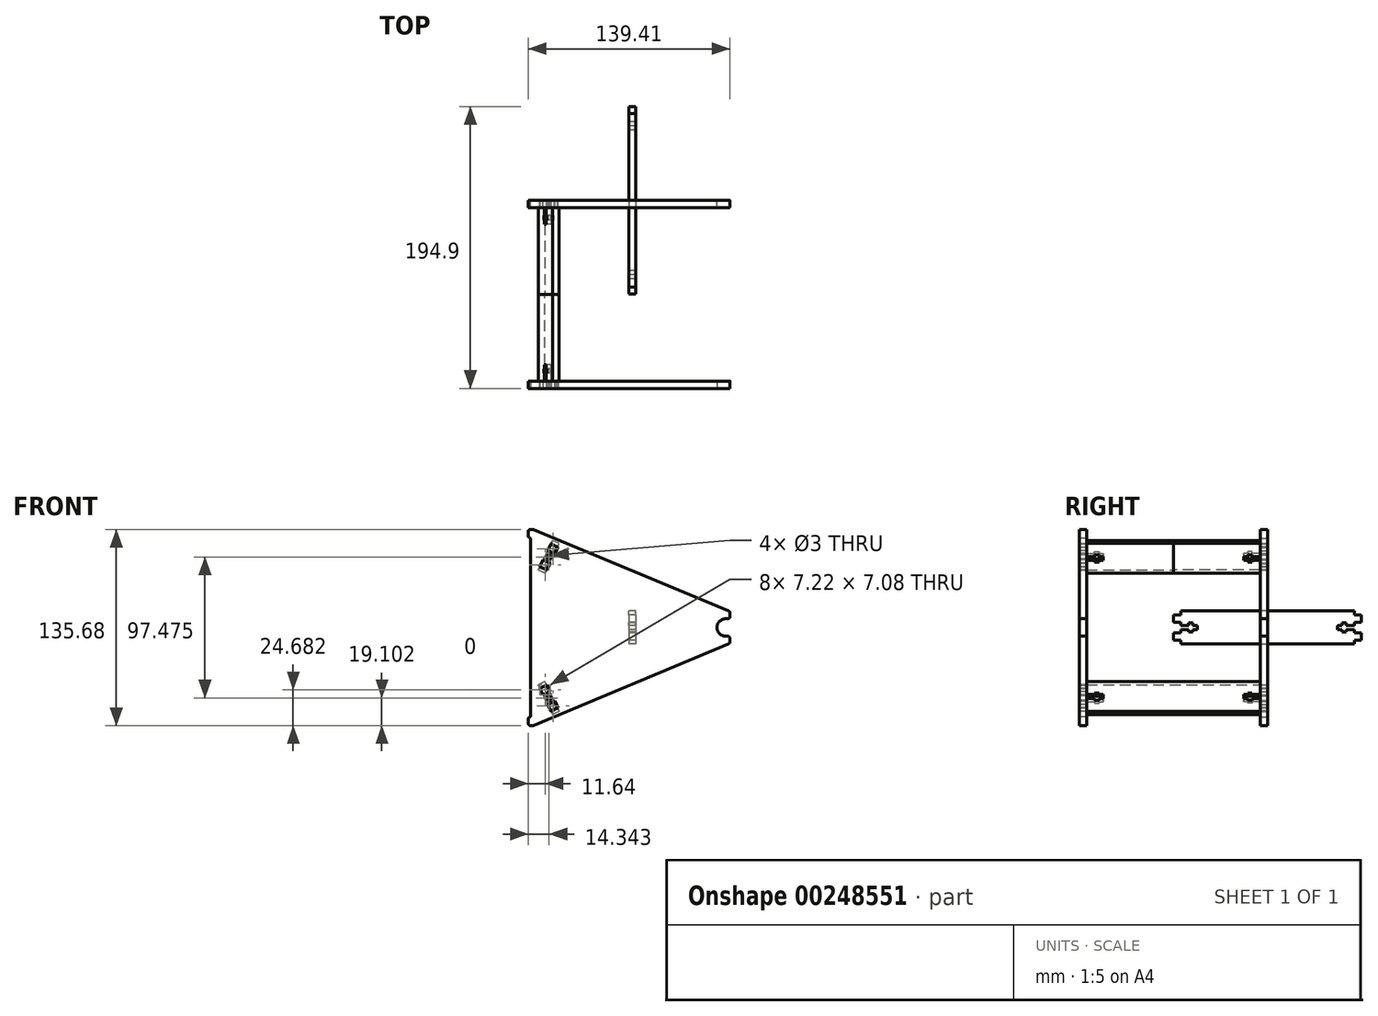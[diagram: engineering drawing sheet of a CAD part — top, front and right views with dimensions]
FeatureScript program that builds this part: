
annotation { "Feature Type Name" : "Feature", "Feature Type Description" : "" }
export const myFeature = defineFeature(function(context is Context, id is Id, definition is map)
    precondition{}
    {
        {
            var Q0;
            Q0=qCreatedBy(makeId("Front.planeOp"),FACE);
            var sketch = newSketch(context, id + "F0", { "sketchPlane" : qUnion([Q0])});
            skLineSegment(sketch, "E0.bottom", {"start": v(70, 69) * mm, "end": v(-70, 69) * mm, "construction": true});
            skLineSegment(sketch, "E0.top", {"start": v(70, -69) * mm, "end": v(-70, -69) * mm, "construction": true});
            skLineSegment(sketch, "E0.left", {"start": v(70, 69) * mm, "end": v(70, -69) * mm, "construction": true});
            skLineSegment(sketch, "E0.right", {"start": v(-70, 69) * mm, "end": v(-70, -69) * mm, "construction": true});
            skPoint(sketch, "E0.middle", {"position": v(0, 0) * mm});
            skLineSegment(sketch, "E1", {"start": v(-67.9, 67.84) * mm, "end": v(-66.66, 67.84) * mm});
            skLineSegment(sketch, "E2", {"start": v(-66.08, 67.72) * mm, "end": v(69.08, 11.47) * mm});
            skArc(sketch, "E3", {"start": v(67, 6) * mm, "mid": v(62.76, 4.24) * mm, "end": v(61, 0) * mm});
            skLineSegment(sketch, "E4", {"start": v(67, 6) * mm, "end": v(68.5, 6) * mm});
            skLineSegment(sketch, "E5", {"start": v(70, 7.5) * mm, "end": v(70, 10.09) * mm});
            skLineSegment(sketch, "E6", {"start": v(73.6, 0) * mm, "end": v(46.28, 0) * mm, "construction": true});
            skPoint(sketch, "E6.startSnap0", {"position": v(70, 0) * mm});
            skCircle(sketch, "E7", {"center": v(67, 0) * mm, "radius": 6 * mm, "construction": true});
            skCircle(sketch, "E8", {"center": v(45.57, 0) * mm, "radius": 27.5 * mm, "construction": true});
            skCircle(sketch, "E9", {"center": v(45.57, 0) * mm, "radius": 100 * mm, "construction": true});
            skLineSegment(sketch, "E10", {"start": v(-69.4, 66.34) * mm, "end": v(-69.4, 63.34) * mm});
            skLineSegment(sketch, "E11", {"start": v(-67.9, 61.84) * mm, "end": v(-67.9, 61.84) * mm});
            skLineSegment(sketch, "E12", {"start": v(-67.9, 61.84) * mm, "end": v(-67.9, 0) * mm});
            skPoint(sketch, "E13.visualSharp", {"position": v(70, 11.09) * mm});
            skArc(sketch, "E13.filletArc", {"start": v(70, 10.09) * mm, "mid": v(69.75, 10.92) * mm, "end": v(69.08, 11.47) * mm});
            skPoint(sketch, "E14.visualSharp", {"position": v(70, 6) * mm});
            skArc(sketch, "E14.filletArc", {"start": v(68.5, 6) * mm, "mid": v(69.56, 6.44) * mm, "end": v(70, 7.5) * mm});
            skPoint(sketch, "E15.visualSharp", {"position": v(-69.4, 67.84) * mm});
            skArc(sketch, "E15.filletArc", {"start": v(-67.9, 67.84) * mm, "mid": v(-68.97, 67.4) * mm, "end": v(-69.4, 66.34) * mm});
            skPoint(sketch, "E16.visualSharp", {"position": v(-69.4, 61.84) * mm});
            skArc(sketch, "E16.filletArc", {"start": v(-69.4, 63.34) * mm, "mid": v(-68.97, 62.27) * mm, "end": v(-67.9, 61.84) * mm});
            skPoint(sketch, "E17.visualSharp", {"position": v(-66.36, 67.84) * mm});
            skArc(sketch, "E17.filletArc", {"start": v(-66.08, 67.72) * mm, "mid": v(-66.37, 67.8) * mm, "end": v(-66.66, 67.84) * mm});
            skLineSegment(sketch, "E18", {"start": v(-48.76, 55.46) * mm, "end": v(-51.02, 50.78) * mm});
            skLineSegment(sketch, "E19", {"start": v(-37.94, 57) * mm, "end": v(-56.8, 18.07) * mm, "construction": true});
            skLineSegment(sketch, "E20", {"start": v(-48.76, 55.46) * mm, "end": v(-53.7, 57.86) * mm});
            skLineSegment(sketch, "E21", {"start": v(-56.43, 39.62) * mm, "end": v(-61.38, 42.02) * mm});
            skLineSegment(sketch, "E22", {"start": v(-53.7, 57.86) * mm, "end": v(-55.97, 53.18) * mm});
            skLineSegment(sketch, "E23", {"start": v(-57.54, 49.94) * mm, "end": v(-52.6, 47.54) * mm, "construction": true});
            skCircle(sketch, "E24", {"center": v(-55.07, 48.74) * mm, "radius": 1.5 * mm});
            skLineSegment(sketch, "E25", {"start": v(-55.97, 53.18) * mm, "end": v(-51.02, 50.78) * mm});
            skLineSegment(sketch, "E26.MirrorCS", {"start": v(-59.11, 46.7) * mm, "end": v(-54.16, 44.3) * mm});
            skLineSegment(sketch, "E27.trimOffspring", {"start": v(-54.16, 44.3) * mm, "end": v(-56.43, 39.62) * mm});
            skLineSegment(sketch, "E28.trimOffspring", {"start": v(-59.11, 46.7) * mm, "end": v(-61.38, 42.02) * mm});
            skLineSegment(sketch, "E29.MirrorCS", {"start": v(-66.08, -67.72) * mm, "end": v(69.08, -11.47) * mm});
            skArc(sketch, "E30.MirrorCS", {"start": v(-66.08, -67.72) * mm, "mid": v(-66.37, -67.8) * mm, "end": v(-66.66, -67.84) * mm});
            skLineSegment(sketch, "E31.MirrorCS", {"start": v(-67.9, -67.84) * mm, "end": v(-66.66, -67.84) * mm});
            skArc(sketch, "E32.MirrorCS", {"start": v(-67.9, -67.84) * mm, "mid": v(-68.97, -67.4) * mm, "end": v(-69.4, -66.34) * mm});
            skLineSegment(sketch, "E33.MirrorCS", {"start": v(-69.4, -66.34) * mm, "end": v(-69.4, -63.34) * mm});
            skArc(sketch, "E34.MirrorCS", {"start": v(-69.4, -63.34) * mm, "mid": v(-68.97, -62.27) * mm, "end": v(-67.9, -61.84) * mm});
            skLineSegment(sketch, "E35.MirrorCS", {"start": v(-67.9, -61.84) * mm, "end": v(-67.9, 0) * mm});
            skLineSegment(sketch, "E36.MirrorCS", {"start": v(70, -7.5) * mm, "end": v(70, -10.09) * mm});
            skArc(sketch, "E37.MirrorCS", {"start": v(70, -10.09) * mm, "mid": v(69.75, -10.92) * mm, "end": v(69.08, -11.47) * mm});
            skArc(sketch, "E38.MirrorCS", {"start": v(68.5, -6) * mm, "mid": v(69.56, -6.44) * mm, "end": v(70, -7.5) * mm});
            skLineSegment(sketch, "E39.MirrorCS", {"start": v(67, -6) * mm, "end": v(68.5, -6) * mm});
            skArc(sketch, "E40.MirrorCS", {"start": v(67, -6) * mm, "mid": v(62.76, -4.24) * mm, "end": v(61, 0) * mm});
            skLineSegment(sketch, "E41.MirrorCS", {"start": v(-57.54, -49.94) * mm, "end": v(-52.6, -47.54) * mm, "construction": true});
            skLineSegment(sketch, "E42.MirrorCS", {"start": v(-59.11, -46.7) * mm, "end": v(-61.38, -42.02) * mm});
            skLineSegment(sketch, "E43.MirrorCS", {"start": v(-53.7, -57.86) * mm, "end": v(-55.97, -53.18) * mm});
            skLineSegment(sketch, "E44.MirrorCS", {"start": v(-59.11, -46.7) * mm, "end": v(-54.16, -44.3) * mm});
            skLineSegment(sketch, "E45.MirrorCS", {"start": v(-55.97, -53.18) * mm, "end": v(-51.02, -50.78) * mm});
            skLineSegment(sketch, "E46.MirrorCS", {"start": v(-56.43, -39.62) * mm, "end": v(-61.38, -42.02) * mm});
            skCircle(sketch, "E47.MirrorC", {"center": v(-55.07, -48.74) * mm, "radius": 1.5 * mm});
            skLineSegment(sketch, "E48.MirrorCS", {"start": v(-48.76, -55.46) * mm, "end": v(-51.02, -50.78) * mm});
            skLineSegment(sketch, "E49.MirrorCS", {"start": v(-54.16, -44.3) * mm, "end": v(-56.43, -39.62) * mm});
            skLineSegment(sketch, "E50.MirrorCS", {"start": v(-48.76, -55.46) * mm, "end": v(-53.7, -57.86) * mm});
            skLineSegment(sketch, "E51", {"start": v(-48.76, 55.46) * mm, "end": v(-56.43, 39.62) * mm, "construction": true});
            skLineSegment(sketch, "E52", {"start": v(-52.6, 47.54) * mm, "end": v(45.57, 0) * mm, "construction": true});
            skSolve(sketch);
        }
        {
            var Q0;
            Q0=qSketchRegion(id+"F0",true);
            extrude(context, id + "F1", {"entities" : qUnion([Q0]), "depth" : 5 * mm});
        }
        {
            var Q0;
            Q0=makeQuery(id+"F1.opExtrude","SWEPT_FACE",FACE,{"disambiguationData":[OSD([sQuery(id+"F0.wireOp",EDGE,"E43.MirrorCS")])]});
            var sketch = newSketch(context, id + "F2", { "sketchPlane" : qUnion([Q0])});
            skLineSegment(sketch, "E53", {"start": v(0, 0) * mm, "end": v(6.16, 29.6) * mm, "construction": true});
            skPoint(sketch, "E53.endSnap0", {"position": v(0, 29.6) * mm});
            skLineSegment(sketch, "E54.0", {"start": v(0, -18.36) * mm, "end": v(0, -21.36) * mm, "construction": true});
            skLineSegment(sketch, "E55", {"start": v(0, -19.86) * mm, "end": v(-5.02, -19.86) * mm, "construction": true});
            skLineSegment(sketch, "E56.1", {"start": v(-0.1, -16.16) * mm, "end": v(-0.1, -11.16) * mm});
            skLineSegment(sketch, "E56.2", {"start": v(-5, -16.16) * mm, "end": v(-0.1, -16.16) * mm});
            skLineSegment(sketch, "E57", {"start": v(-5, -16.16) * mm, "end": v(-5, -18.36) * mm});
            skLineSegment(sketch, "E58", {"start": v(-5, -18.36) * mm, "end": v(-10.6, -18.36) * mm});
            skLineSegment(sketch, "E59", {"start": v(-10.6, -18.36) * mm, "end": v(-10.6, -17.09) * mm});
            skLineSegment(sketch, "E60", {"start": v(-10.6, -17.09) * mm, "end": v(-13.5, -17.09) * mm});
            skLineSegment(sketch, "E61", {"start": v(-13.5, -17.09) * mm, "end": v(-13.5, -18.36) * mm});
            skLineSegment(sketch, "E62", {"start": v(-13.5, -18.36) * mm, "end": v(-16.5, -18.36) * mm});
            skLineSegment(sketch, "E63", {"start": v(-16.5, -18.36) * mm, "end": v(-16.5, -19.86) * mm});
            skLineSegment(sketch, "E64", {"start": v(-0.1, -11.16) * mm, "end": v(-5, -11.16) * mm});
            skLineSegment(sketch, "E65", {"start": v(-5, -11.16) * mm, "end": v(-5, -8.44) * mm});
            skLineSegment(sketch, "E66", {"start": v(-5, -8.44) * mm, "end": v(-65, -8.44) * mm});
            skLineSegment(sketch, "E67.MirrorCS", {"start": v(-13.5, -21.36) * mm, "end": v(-16.5, -21.36) * mm});
            skLineSegment(sketch, "E68.MirrorCS", {"start": v(-10.6, -21.36) * mm, "end": v(-10.6, -22.64) * mm});
            skLineSegment(sketch, "E69.MirrorCS", {"start": v(-5, -28.56) * mm, "end": v(-5, -31.28) * mm});
            skLineSegment(sketch, "E70.MirrorCS", {"start": v(-16.5, -21.36) * mm, "end": v(-16.5, -19.86) * mm});
            skLineSegment(sketch, "E71.MirrorCS", {"start": v(-5, -23.56) * mm, "end": v(-5, -21.36) * mm});
            skLineSegment(sketch, "E72.MirrorCS", {"start": v(-13.5, -22.64) * mm, "end": v(-13.5, -21.36) * mm});
            skLineSegment(sketch, "E73.MirrorCS", {"start": v(-10.6, -22.64) * mm, "end": v(-13.5, -22.64) * mm});
            skLineSegment(sketch, "E74.MirrorCS", {"start": v(0, -21.36) * mm, "end": v(0, -18.36) * mm, "construction": true});
            skLineSegment(sketch, "E75.MirrorCS", {"start": v(-5, -31.28) * mm, "end": v(-65, -31.28) * mm});
            skLineSegment(sketch, "E76.MirrorCS", {"start": v(-0.1, -23.56) * mm, "end": v(-0.1, -28.56) * mm});
            skLineSegment(sketch, "E77.MirrorCS", {"start": v(-5, -21.36) * mm, "end": v(-10.6, -21.36) * mm});
            skLineSegment(sketch, "E78.MirrorCS", {"start": v(-0.1, -28.56) * mm, "end": v(-5, -28.56) * mm});
            skLineSegment(sketch, "E79.MirrorCS", {"start": v(-5, -23.56) * mm, "end": v(-0.1, -23.56) * mm});
            skLineSegment(sketch, "E80", {"start": v(-65, -8.44) * mm, "end": v(-65, -31.28) * mm});
            skSolve(sketch);
        }
        {
            var Q0;
            Q0=qSketchRegion(id+"F2",true);
            extrude(context, id + "F3", {"entities" : qUnion([Q0]), "depth" : 5 * mm});
        }
        {
            var Q0;
            Q0=makeQuery(id+"F3.opExtrude","SWEPT_BODY",BODY,{"disambiguationData":[OSD([sQuery(id+"F2.wireOp",EDGE,"E56.1"),sQuery(id+"F2.wireOp",EDGE,"E56.2"),sQuery(id+"F2.wireOp",EDGE,"E57"),sQuery(id+"F2.wireOp",EDGE,"E58"),sQuery(id+"F2.wireOp",EDGE,"E59"),sQuery(id+"F2.wireOp",EDGE,"E60"),sQuery(id+"F2.wireOp",EDGE,"E61"),sQuery(id+"F2.wireOp",EDGE,"E62"),sQuery(id+"F2.wireOp",EDGE,"E63"),sQuery(id+"F2.wireOp",EDGE,"E64"),sQuery(id+"F2.wireOp",EDGE,"E65"),sQuery(id+"F2.wireOp",EDGE,"E66"),sQuery(id+"F2.wireOp",EDGE,"E67.MirrorCS"),sQuery(id+"F2.wireOp",EDGE,"E68.MirrorCS"),sQuery(id+"F2.wireOp",EDGE,"E69.MirrorCS"),sQuery(id+"F2.wireOp",EDGE,"E70.MirrorCS"),sQuery(id+"F2.wireOp",EDGE,"E71.MirrorCS"),sQuery(id+"F2.wireOp",EDGE,"E72.MirrorCS"),sQuery(id+"F2.wireOp",EDGE,"E73.MirrorCS"),sQuery(id+"F2.wireOp",EDGE,"E75.MirrorCS"),sQuery(id+"F2.wireOp",EDGE,"E76.MirrorCS"),sQuery(id+"F2.wireOp",EDGE,"E77.MirrorCS"),sQuery(id+"F2.wireOp",EDGE,"E78.MirrorCS"),sQuery(id+"F2.wireOp",EDGE,"E79.MirrorCS"),sQuery(id+"F2.wireOp",EDGE,"E80")])]});
            var Q1;
            Q1=qCreatedBy(makeId("Top.planeOp"),FACE);
            mirror(context, id + "F4", {"entities" : qUnion([Q0]), "mirrorPlane" : qUnion([Q1])});
        }
        {
            var Q0;
            Q0=makeQuery(id+"F1.opExtrude","SWEPT_BODY",BODY,{"disambiguationData":[OSD([sQuery(id+"F0.wireOp",EDGE,"E1"),sQuery(id+"F0.wireOp",EDGE,"E2"),sQuery(id+"F0.wireOp",EDGE,"E3"),sQuery(id+"F0.wireOp",EDGE,"E4"),sQuery(id+"F0.wireOp",EDGE,"E5"),sQuery(id+"F0.wireOp",EDGE,"E10"),sQuery(id+"F0.wireOp",EDGE,"E12"),sQuery(id+"F0.wireOp",EDGE,"E13.filletArc"),sQuery(id+"F0.wireOp",EDGE,"E14.filletArc"),sQuery(id+"F0.wireOp",EDGE,"E15.filletArc"),sQuery(id+"F0.wireOp",EDGE,"E16.filletArc"),sQuery(id+"F0.wireOp",EDGE,"E17.filletArc"),sQuery(id+"F0.wireOp",EDGE,"E18"),sQuery(id+"F0.wireOp",EDGE,"E20"),sQuery(id+"F0.wireOp",EDGE,"E21"),sQuery(id+"F0.wireOp",EDGE,"E22"),sQuery(id+"F0.wireOp",EDGE,"E24"),sQuery(id+"F0.wireOp",EDGE,"E25"),sQuery(id+"F0.wireOp",EDGE,"E26.MirrorCS"),sQuery(id+"F0.wireOp",EDGE,"E27.trimOffspring"),sQuery(id+"F0.wireOp",EDGE,"E28.trimOffspring"),sQuery(id+"F0.wireOp",EDGE,"E29.MirrorCS"),sQuery(id+"F0.wireOp",EDGE,"E30.MirrorCS"),sQuery(id+"F0.wireOp",EDGE,"E31.MirrorCS"),sQuery(id+"F0.wireOp",EDGE,"E32.MirrorCS"),sQuery(id+"F0.wireOp",EDGE,"E33.MirrorCS"),sQuery(id+"F0.wireOp",EDGE,"E34.MirrorCS"),sQuery(id+"F0.wireOp",EDGE,"E35.MirrorCS"),sQuery(id+"F0.wireOp",EDGE,"E36.MirrorCS"),sQuery(id+"F0.wireOp",EDGE,"E37.MirrorCS"),sQuery(id+"F0.wireOp",EDGE,"E38.MirrorCS"),sQuery(id+"F0.wireOp",EDGE,"E39.MirrorCS"),sQuery(id+"F0.wireOp",EDGE,"E40.MirrorCS"),sQuery(id+"F0.wireOp",EDGE,"E42.MirrorCS"),sQuery(id+"F0.wireOp",EDGE,"E43.MirrorCS"),sQuery(id+"F0.wireOp",EDGE,"E44.MirrorCS"),sQuery(id+"F0.wireOp",EDGE,"E45.MirrorCS"),sQuery(id+"F0.wireOp",EDGE,"E46.MirrorCS"),sQuery(id+"F0.wireOp",EDGE,"E47.MirrorC"),sQuery(id+"F0.wireOp",EDGE,"E48.MirrorCS"),sQuery(id+"F0.wireOp",EDGE,"E49.MirrorCS"),sQuery(id+"F0.wireOp",EDGE,"E50.MirrorCS")])]});
            var Q1;
            Q1=makeQuery(id+"F3.opExtrude","SWEPT_BODY",BODY,{"disambiguationData":[OSD([sQuery(id+"F2.wireOp",EDGE,"E56.1"),sQuery(id+"F2.wireOp",EDGE,"E56.2"),sQuery(id+"F2.wireOp",EDGE,"E57"),sQuery(id+"F2.wireOp",EDGE,"E58"),sQuery(id+"F2.wireOp",EDGE,"E59"),sQuery(id+"F2.wireOp",EDGE,"E60"),sQuery(id+"F2.wireOp",EDGE,"E61"),sQuery(id+"F2.wireOp",EDGE,"E62"),sQuery(id+"F2.wireOp",EDGE,"E63"),sQuery(id+"F2.wireOp",EDGE,"E64"),sQuery(id+"F2.wireOp",EDGE,"E65"),sQuery(id+"F2.wireOp",EDGE,"E66"),sQuery(id+"F2.wireOp",EDGE,"E67.MirrorCS"),sQuery(id+"F2.wireOp",EDGE,"E68.MirrorCS"),sQuery(id+"F2.wireOp",EDGE,"E69.MirrorCS"),sQuery(id+"F2.wireOp",EDGE,"E70.MirrorCS"),sQuery(id+"F2.wireOp",EDGE,"E71.MirrorCS"),sQuery(id+"F2.wireOp",EDGE,"E72.MirrorCS"),sQuery(id+"F2.wireOp",EDGE,"E73.MirrorCS"),sQuery(id+"F2.wireOp",EDGE,"E75.MirrorCS"),sQuery(id+"F2.wireOp",EDGE,"E76.MirrorCS"),sQuery(id+"F2.wireOp",EDGE,"E77.MirrorCS"),sQuery(id+"F2.wireOp",EDGE,"E78.MirrorCS"),sQuery(id+"F2.wireOp",EDGE,"E79.MirrorCS"),sQuery(id+"F2.wireOp",EDGE,"E80")])]});
            var Q2;
            Q2=makeQuery(id+"F4.opPattern","COPY",BODY,{"derivedFrom":makeQuery(id+"F3.opExtrude","SWEPT_BODY",BODY,{"disambiguationData":[OSD([sQuery(id+"F2.wireOp",EDGE,"E56.1"),sQuery(id+"F2.wireOp",EDGE,"E56.2"),sQuery(id+"F2.wireOp",EDGE,"E57"),sQuery(id+"F2.wireOp",EDGE,"E58"),sQuery(id+"F2.wireOp",EDGE,"E59"),sQuery(id+"F2.wireOp",EDGE,"E60"),sQuery(id+"F2.wireOp",EDGE,"E61"),sQuery(id+"F2.wireOp",EDGE,"E62"),sQuery(id+"F2.wireOp",EDGE,"E63"),sQuery(id+"F2.wireOp",EDGE,"E64"),sQuery(id+"F2.wireOp",EDGE,"E65"),sQuery(id+"F2.wireOp",EDGE,"E66"),sQuery(id+"F2.wireOp",EDGE,"E67.MirrorCS"),sQuery(id+"F2.wireOp",EDGE,"E68.MirrorCS"),sQuery(id+"F2.wireOp",EDGE,"E69.MirrorCS"),sQuery(id+"F2.wireOp",EDGE,"E70.MirrorCS"),sQuery(id+"F2.wireOp",EDGE,"E71.MirrorCS"),sQuery(id+"F2.wireOp",EDGE,"E72.MirrorCS"),sQuery(id+"F2.wireOp",EDGE,"E73.MirrorCS"),sQuery(id+"F2.wireOp",EDGE,"E75.MirrorCS"),sQuery(id+"F2.wireOp",EDGE,"E76.MirrorCS"),sQuery(id+"F2.wireOp",EDGE,"E77.MirrorCS"),sQuery(id+"F2.wireOp",EDGE,"E78.MirrorCS"),sQuery(id+"F2.wireOp",EDGE,"E79.MirrorCS"),sQuery(id+"F2.wireOp",EDGE,"E80")])]}),"instanceName":"1"});
            var Q3;
            Q3=makeQuery(id+"F4.opPattern","COPY",FACE,{"derivedFrom":makeQuery(id+"F3.opExtrude","SWEPT_FACE",FACE,{"disambiguationData":[OSD([sQuery(id+"F2.wireOp",EDGE,"E80")])]}),"instanceName":"1"});
            mirror(context, id + "F5", {"entities" : qUnion([Q0, Q1, Q2]), "mirrorPlane" : qUnion([Q3])});
        }
        {
            var Q0;
            Q0=makeQuery(id+"F5.opPattern","COPY",BODY,{"derivedFrom":makeQuery(id+"F3.opExtrude","SWEPT_BODY",BODY,{"disambiguationData":[OSD([sQuery(id+"F2.wireOp",EDGE,"E56.1"),sQuery(id+"F2.wireOp",EDGE,"E56.2"),sQuery(id+"F2.wireOp",EDGE,"E57"),sQuery(id+"F2.wireOp",EDGE,"E58"),sQuery(id+"F2.wireOp",EDGE,"E59"),sQuery(id+"F2.wireOp",EDGE,"E60"),sQuery(id+"F2.wireOp",EDGE,"E61"),sQuery(id+"F2.wireOp",EDGE,"E62"),sQuery(id+"F2.wireOp",EDGE,"E63"),sQuery(id+"F2.wireOp",EDGE,"E64"),sQuery(id+"F2.wireOp",EDGE,"E65"),sQuery(id+"F2.wireOp",EDGE,"E66"),sQuery(id+"F2.wireOp",EDGE,"E67.MirrorCS"),sQuery(id+"F2.wireOp",EDGE,"E68.MirrorCS"),sQuery(id+"F2.wireOp",EDGE,"E69.MirrorCS"),sQuery(id+"F2.wireOp",EDGE,"E70.MirrorCS"),sQuery(id+"F2.wireOp",EDGE,"E71.MirrorCS"),sQuery(id+"F2.wireOp",EDGE,"E72.MirrorCS"),sQuery(id+"F2.wireOp",EDGE,"E73.MirrorCS"),sQuery(id+"F2.wireOp",EDGE,"E75.MirrorCS"),sQuery(id+"F2.wireOp",EDGE,"E76.MirrorCS"),sQuery(id+"F2.wireOp",EDGE,"E77.MirrorCS"),sQuery(id+"F2.wireOp",EDGE,"E78.MirrorCS"),sQuery(id+"F2.wireOp",EDGE,"E79.MirrorCS"),sQuery(id+"F2.wireOp",EDGE,"E80")])]}),"instanceName":"1"});
            var Q1;
            Q1=makeQuery(id+"F3.opExtrude","SWEPT_BODY",BODY,{"disambiguationData":[OSD([sQuery(id+"F2.wireOp",EDGE,"E56.1"),sQuery(id+"F2.wireOp",EDGE,"E56.2"),sQuery(id+"F2.wireOp",EDGE,"E57"),sQuery(id+"F2.wireOp",EDGE,"E58"),sQuery(id+"F2.wireOp",EDGE,"E59"),sQuery(id+"F2.wireOp",EDGE,"E60"),sQuery(id+"F2.wireOp",EDGE,"E61"),sQuery(id+"F2.wireOp",EDGE,"E62"),sQuery(id+"F2.wireOp",EDGE,"E63"),sQuery(id+"F2.wireOp",EDGE,"E64"),sQuery(id+"F2.wireOp",EDGE,"E65"),sQuery(id+"F2.wireOp",EDGE,"E66"),sQuery(id+"F2.wireOp",EDGE,"E67.MirrorCS"),sQuery(id+"F2.wireOp",EDGE,"E68.MirrorCS"),sQuery(id+"F2.wireOp",EDGE,"E69.MirrorCS"),sQuery(id+"F2.wireOp",EDGE,"E70.MirrorCS"),sQuery(id+"F2.wireOp",EDGE,"E71.MirrorCS"),sQuery(id+"F2.wireOp",EDGE,"E72.MirrorCS"),sQuery(id+"F2.wireOp",EDGE,"E73.MirrorCS"),sQuery(id+"F2.wireOp",EDGE,"E75.MirrorCS"),sQuery(id+"F2.wireOp",EDGE,"E76.MirrorCS"),sQuery(id+"F2.wireOp",EDGE,"E77.MirrorCS"),sQuery(id+"F2.wireOp",EDGE,"E78.MirrorCS"),sQuery(id+"F2.wireOp",EDGE,"E79.MirrorCS"),sQuery(id+"F2.wireOp",EDGE,"E80")])]});
            booleanBodies(context, id + "F6", {"operationType" : BooleanOperationType.UNION, "tools" : qUnion([Q0, Q1])});
        }
        {
            var Q0;
            Q0=qCreatedBy(makeId("Right.planeOp"),FACE);
            var sketch = newSketch(context, id + "F7", { "sketchPlane" : qUnion([Q0])});
            skLineSegment(sketch, "E81.0.0", {"start": v(-64.9, 3.7) * mm, "end": v(-60, 3.7) * mm});
            skLineSegment(sketch, "E81.0.1", {"start": v(-60, 3.7) * mm, "end": v(-60, 1.5) * mm});
            skLineSegment(sketch, "E81.0.2", {"start": v(-60, 1.5) * mm, "end": v(-54.4, 1.5) * mm});
            skLineSegment(sketch, "E81.0.3", {"start": v(-54.4, 1.5) * mm, "end": v(-54.4, 3.18) * mm});
            skLineSegment(sketch, "E81.0.4", {"start": v(-54.4, 3.18) * mm, "end": v(-51.5, 3.18) * mm});
            skLineSegment(sketch, "E81.0.5", {"start": v(-51.5, 3.18) * mm, "end": v(-51.5, 1.5) * mm});
            skLineSegment(sketch, "E81.0.6", {"start": v(-51.5, 1.5) * mm, "end": v(-48.5, 1.5) * mm});
            skLineSegment(sketch, "E81.0.7", {"start": v(-48.5, 1.5) * mm, "end": v(-48.5, -1.5) * mm});
            skLineSegment(sketch, "E81.0.8", {"start": v(-48.5, -1.5) * mm, "end": v(-51.5, -1.5) * mm});
            skLineSegment(sketch, "E81.0.9", {"start": v(-51.5, -1.5) * mm, "end": v(-51.5, -3.18) * mm});
            skLineSegment(sketch, "E81.0.10", {"start": v(-51.5, -3.18) * mm, "end": v(-54.4, -3.18) * mm});
            skLineSegment(sketch, "E81.0.11", {"start": v(-54.4, -3.18) * mm, "end": v(-54.4, -1.5) * mm});
            skLineSegment(sketch, "E81.0.12", {"start": v(-54.4, -1.5) * mm, "end": v(-60, -1.5) * mm});
            skLineSegment(sketch, "E81.0.13", {"start": v(-60, -1.5) * mm, "end": v(-60, -3.7) * mm});
            skLineSegment(sketch, "E81.0.14", {"start": v(-60, -3.7) * mm, "end": v(-64.9, -3.7) * mm});
            skLineSegment(sketch, "E81.0.15", {"start": v(-64.9, -3.7) * mm, "end": v(-64.9, -8.7) * mm});
            skLineSegment(sketch, "E81.0.16", {"start": v(-64.9, -8.7) * mm, "end": v(-60, -8.7) * mm});
            skLineSegment(sketch, "E81.0.17", {"start": v(-60, -8.7) * mm, "end": v(-60, -11.42) * mm});
            skLineSegment(sketch, "E81.0.18", {"start": v(-60, -11.42) * mm, "end": v(60, -11.42) * mm});
            skLineSegment(sketch, "E81.0.19", {"start": v(60, -11.42) * mm, "end": v(60, -8.7) * mm});
            skLineSegment(sketch, "E81.0.20", {"start": v(60, -8.7) * mm, "end": v(64.9, -8.7) * mm});
            skLineSegment(sketch, "E81.0.21", {"start": v(64.9, -8.7) * mm, "end": v(64.9, -3.7) * mm});
            skLineSegment(sketch, "E81.0.22", {"start": v(64.9, -3.7) * mm, "end": v(60, -3.7) * mm});
            skLineSegment(sketch, "E81.0.23", {"start": v(60, -3.7) * mm, "end": v(60, -1.5) * mm});
            skLineSegment(sketch, "E81.0.24", {"start": v(60, -1.5) * mm, "end": v(54.4, -1.5) * mm});
            skLineSegment(sketch, "E81.0.25", {"start": v(54.4, -1.5) * mm, "end": v(54.4, -3.18) * mm});
            skLineSegment(sketch, "E81.0.26", {"start": v(54.4, -3.18) * mm, "end": v(51.5, -3.18) * mm});
            skLineSegment(sketch, "E81.0.27", {"start": v(51.5, -3.18) * mm, "end": v(51.5, -1.5) * mm});
            skLineSegment(sketch, "E81.0.28", {"start": v(51.5, -1.5) * mm, "end": v(48.5, -1.5) * mm});
            skLineSegment(sketch, "E81.0.29", {"start": v(48.5, -1.5) * mm, "end": v(48.5, 1.5) * mm});
            skLineSegment(sketch, "E81.0.30", {"start": v(48.5, 1.5) * mm, "end": v(51.5, 1.5) * mm});
            skLineSegment(sketch, "E81.0.31", {"start": v(51.5, 1.5) * mm, "end": v(51.5, 3.18) * mm});
            skLineSegment(sketch, "E81.0.32", {"start": v(51.5, 3.18) * mm, "end": v(54.4, 3.18) * mm});
            skLineSegment(sketch, "E81.0.33", {"start": v(54.4, 3.18) * mm, "end": v(54.4, 1.5) * mm});
            skLineSegment(sketch, "E81.0.34", {"start": v(54.4, 1.5) * mm, "end": v(60, 1.5) * mm});
            skLineSegment(sketch, "E81.0.35", {"start": v(60, 1.5) * mm, "end": v(60, 3.7) * mm});
            skLineSegment(sketch, "E81.0.36", {"start": v(60, 3.7) * mm, "end": v(64.9, 3.7) * mm});
            skLineSegment(sketch, "E81.0.37", {"start": v(64.9, 3.7) * mm, "end": v(64.9, 8.7) * mm});
            skLineSegment(sketch, "E81.0.38", {"start": v(64.9, 8.7) * mm, "end": v(60, 8.7) * mm});
            skLineSegment(sketch, "E81.0.39", {"start": v(60, 8.7) * mm, "end": v(60, 11.42) * mm});
            skLineSegment(sketch, "E81.0.40", {"start": v(60, 11.42) * mm, "end": v(-60, 11.42) * mm});
            skLineSegment(sketch, "E81.0.41", {"start": v(-60, 11.42) * mm, "end": v(-60, 8.7) * mm});
            skLineSegment(sketch, "E81.0.42", {"start": v(-60, 8.7) * mm, "end": v(-64.9, 8.7) * mm});
            skLineSegment(sketch, "E81.0.43", {"start": v(-64.9, 8.7) * mm, "end": v(-64.9, 3.7) * mm});
            skSolve(sketch);
        }
        {
            var Q0;
            Q0=makeQuery(id+"F7.imprint","IMPRINT",FACE,{"disambiguationData":[TD([[makeQuery(id+"F7.imprint","IMPRINT",EDGE,{"derivedFrom":sQuery(id+"F7.wireOp",EDGE,"E81.0.0")}),1.0]])]});
            extrude(context, id + "F8", {"entities" : qUnion([Q0]), "depth" : 5 * mm});
        }
    });
